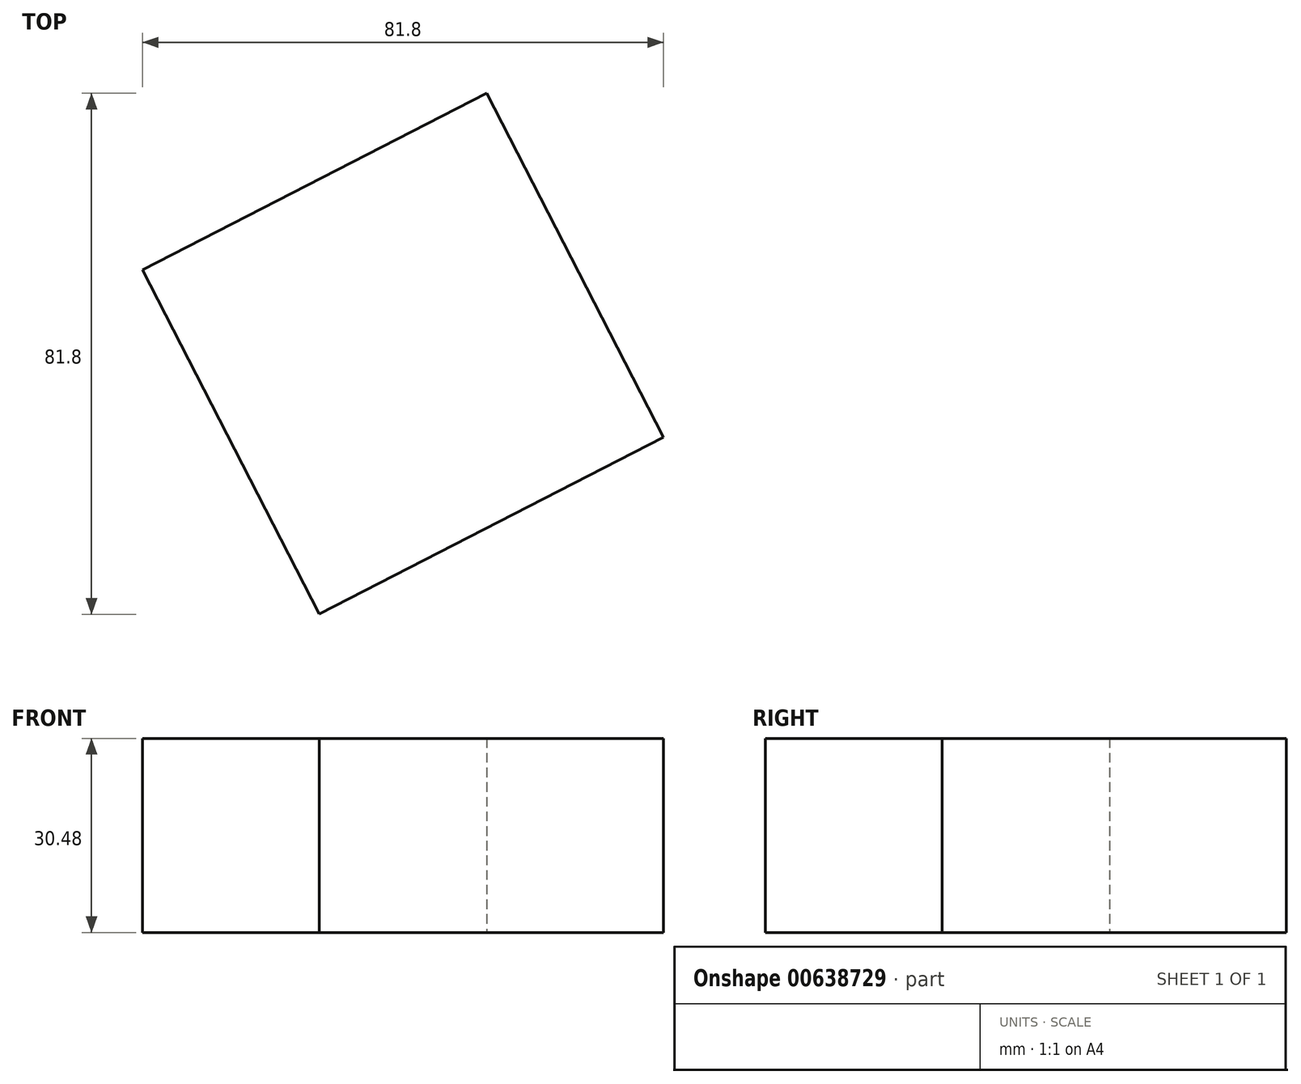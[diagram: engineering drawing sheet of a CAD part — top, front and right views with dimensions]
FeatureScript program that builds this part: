
annotation { "Feature Type Name" : "Feature", "Feature Type Description" : "" }
export const myFeature = defineFeature(function(context is Context, id is Id, definition is map)
    precondition{}
    {
        {
            var Q0;
            Q0=qCreatedBy(makeId("Top.planeOp"),FACE);
            var sketch = newSketch(context, id + "F0", { "sketchPlane" : qUnion([Q0])});
            skCircle(sketch, "E0.cCircle", {"center": v(0, 0) * mm, "radius": 30.38 * mm, "construction": true});
            skLineSegment(sketch, "E0.0", {"start": v(-13.15, -40.9) * mm, "end": v(-40.9, 13.15) * mm});
            skLineSegment(sketch, "E0.1", {"start": v(-40.9, 13.15) * mm, "end": v(13.15, 40.9) * mm});
            skLineSegment(sketch, "E0.2", {"start": v(13.15, 40.9) * mm, "end": v(40.9, -13.15) * mm});
            skLineSegment(sketch, "E0.3", {"start": v(40.9, -13.15) * mm, "end": v(-13.15, -40.9) * mm});
            skPoint(sketch, "E0.0.midPoint", {"position": v(-27.02, -13.88) * mm});
            skSolve(sketch);
        }
        {
            var Q0;
            Q0=makeQuery(id+"F0.imprint","IMPRINT",FACE,{"disambiguationData":[TD([[makeQuery(id+"F0.imprint","IMPRINT",EDGE,{"derivedFrom":sQuery(id+"F0.wireOp",EDGE,"E0.0")}),-1.0]])]});
            extrude(context, id + "F1", {"entities" : qUnion([Q0]), "depth" : 30.48 * mm, "offsetDistance" : 25.4 * mm});
        }
    });
